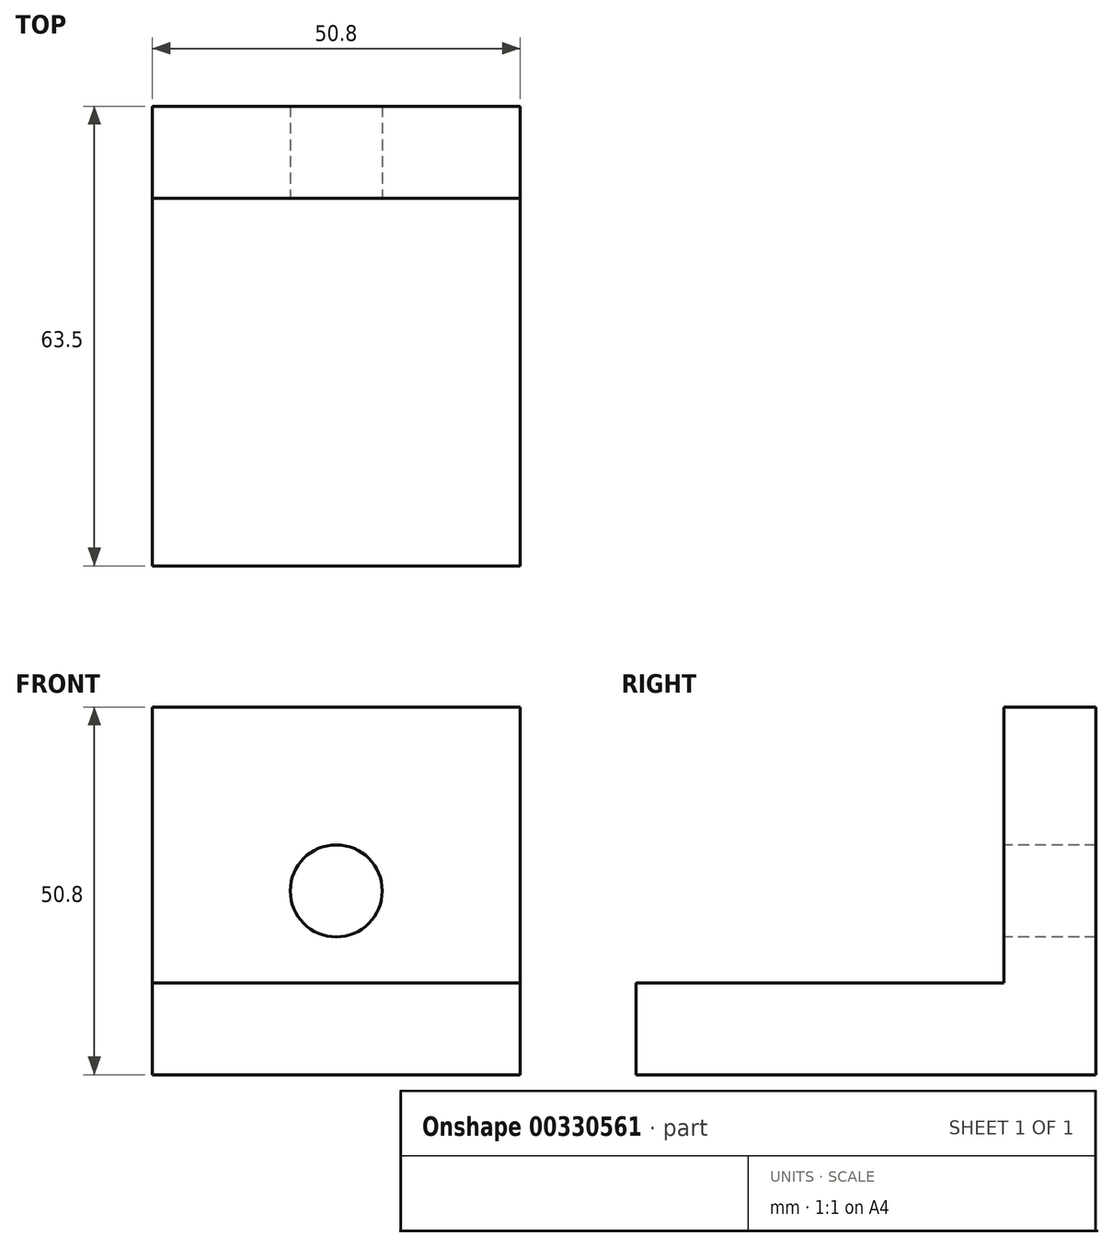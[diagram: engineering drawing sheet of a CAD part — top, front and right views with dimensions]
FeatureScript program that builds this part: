
annotation { "Feature Type Name" : "Feature", "Feature Type Description" : "" }
export const myFeature = defineFeature(function(context is Context, id is Id, definition is map)
    precondition{}
    {
        {
            var Q0;
            Q0=qCreatedBy(makeId("Front.planeOp"),FACE);
            var sketch = newSketch(context, id + "F0", { "sketchPlane" : qUnion([Q0])});
            skLineSegment(sketch, "E0.bottom", {"start": v(-25.4, -25.4) * mm, "end": v(25.4, -25.4) * mm});
            skLineSegment(sketch, "E0.top", {"start": v(-25.4, 25.4) * mm, "end": v(25.4, 25.4) * mm});
            skLineSegment(sketch, "E0.left", {"start": v(-25.4, -25.4) * mm, "end": v(-25.4, 25.4) * mm});
            skLineSegment(sketch, "E0.right", {"start": v(25.4, -25.4) * mm, "end": v(25.4, 25.4) * mm});
            skPoint(sketch, "E0.middle", {"position": v(0, 0) * mm});
            skSolve(sketch);
        }
        {
            var Q0;
            Q0=makeQuery(id+"F0.imprint","IMPRINT",FACE,{"disambiguationData":[TD([[makeQuery(id+"F0.imprint","IMPRINT",EDGE,{"derivedFrom":sQuery(id+"F0.wireOp",EDGE,"E0.bottom")}),1.0]])]});
            extrude(context, id + "F1", {"entities" : qUnion([Q0]), "depth" : 12.7 * mm});
        }
        {
            var Q0;
            Q0=makeQuery(id+"F1.opExtrude","CAP_FACE",FACE,{"disambiguationData":[OSD([sQuery(id+"F0.wireOp",EDGE,"E0.bottom"),sQuery(id+"F0.wireOp",EDGE,"E0.top"),sQuery(id+"F0.wireOp",EDGE,"E0.left"),sQuery(id+"F0.wireOp",EDGE,"E0.right")])],"isStart":false});
            var sketch = newSketch(context, id + "F2", { "sketchPlane" : qUnion([Q0])});
            skLineSegment(sketch, "E1.bottom", {"start": v(-25.4, -25.4) * mm, "end": v(25.4, -25.4) * mm});
            skLineSegment(sketch, "E1.top", {"start": v(-25.4, -12.7) * mm, "end": v(25.4, -12.7) * mm});
            skLineSegment(sketch, "E1.left", {"start": v(-25.4, -25.4) * mm, "end": v(-25.4, -12.7) * mm});
            skLineSegment(sketch, "E1.right", {"start": v(25.4, -25.4) * mm, "end": v(25.4, -12.7) * mm});
            skSolve(sketch);
        }
        {
            var Q0;
            Q0 = qSketchRegion(id + "F2", true);
            extrude(context, id + "F3", {"entities" : qUnion([Q0]), "operationType" : NewBodyOperationType.ADD, "depth" : 50.8 * mm});
        }
        {
            var Q0;
            Q0=makeQuery(id+"F1.opExtrude","CAP_FACE",FACE,{"disambiguationData":[OSD([sQuery(id+"F0.wireOp",EDGE,"E0.bottom"),sQuery(id+"F0.wireOp",EDGE,"E0.top"),sQuery(id+"F0.wireOp",EDGE,"E0.left"),sQuery(id+"F0.wireOp",EDGE,"E0.right")])],"isStart":false});
            var sketch = newSketch(context, id + "F4", { "sketchPlane" : qUnion([Q0])});
            skCircle(sketch, "E2", {"center": v(0, 0) * mm, "radius": 6.35 * mm});
            skSolve(sketch);
        }
        {
            var Q0;
            Q0=makeQuery(id+"F4.imprint","IMPRINT",FACE,{"disambiguationData":[TD([[makeQuery(id+"F4.imprint","IMPRINT",EDGE,{"derivedFrom":sQuery(id+"F4.wireOp",EDGE,"E2")}),1.0]])]});
            extrude(context, id + "F5", {"entities" : qUnion([Q0]), "operationType" : NewBodyOperationType.REMOVE, "endBound" : BoundingType.THROUGH_ALL, "oppositeDirection" : true, "depth" : 25.4 * mm});
        }
    });
